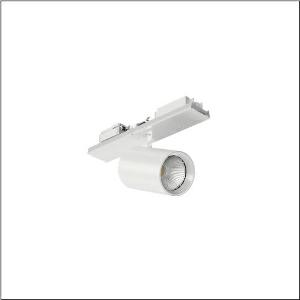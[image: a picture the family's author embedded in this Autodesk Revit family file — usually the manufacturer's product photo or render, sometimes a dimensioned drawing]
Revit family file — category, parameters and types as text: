
# Revit family: licross_r__spot_31_51sl13da45b_aeee
name_source: partatom
category: Lighting Fixtures
units: mm (PartAtom-declared; Revit-internal decimal feet)

## family parameters
Cut with Voids When Loaded = No
Host = Face
Light Source = No
Part Type = Normal
Room Calculation Point = No
Round Connector Dimension = Use Diameter
Shared = No

## types (1)
- --- (1 x LED, 5190 lm, 43.9 W, 4000K)
    Apparent Load = 44 VA
    CIE Flux Codes = 92 97 99 100 100
    Color Rendering = 90
    Color Temperature = 4000K
    Default Elevation = 1800 mm
    Description = Licross® Spot 31, directional spotlight, light control with lens, of plastic, LED rated luminous flux: 5.190lm, light colour: 940, with plug, 5-pole, mains connection: 220..240V, AC, 50/60Hz, of aluminium, traffic white (RAL 9016), length: 140mm, diameter: 90mm, protection rating (complete): IP20, insulation class (complete): insulation class I (protective earthing), certification: CE, packaging unit: 1 piece
    Height = 175 mm
    Lamp = 1 x LED
    Lamp Light Flux = 5190 lm
    Lamp Power = 43.9 W
    Lamp count = 1
    Length = 90 mm
    Luminous efficacy = 118 lm/W
    Manufacturer = Siteco
    ModVariant = No
    Model = 51SL13DA45B
    Mounting Place = Ceiling
    Mounting Type = Pendant
    Number of Poles = 1
    OnlyDefault = Yes
    Power Factor = 1
    Product Name = Licross® Spot 31
    Product group = directional spotlight
    ProductGroupID = 905
    Protection Class = Protection class I
    Protection Degree = IP 20
    RLX_Detail_Level = 1
    RLX_Emergency_Light_Flux = 0 lm
    RLX_Emergency_Type = 0
    RLX_Emergency_Type_DB = No
    RlxData = <blob elided: 14789 chars, md5=d6689394>
    Socket = socket
    Standby Power = 0 W
    System Light Flux = 5190 lm
    System Power = 44 W
    Type Comments = factory setting: luminous flux: 100 % | (ON | ON | ON) | 1050 mA
    Type Image = l_1245720.jpg
    URL = http://relux.com
    VarID = @adj_063783
    Voltage = 0 V
    Weight = 0.00 kg
    Width = 0 mm  [stored 0 ft]

note: [stored X ft] marks values corroborated as IEEE doubles in the binary element streams (Revit-internal decimal feet)

## geometry (parser evidence)
native form markers: Sweep x11
no freeform markers — native parametric forms only
